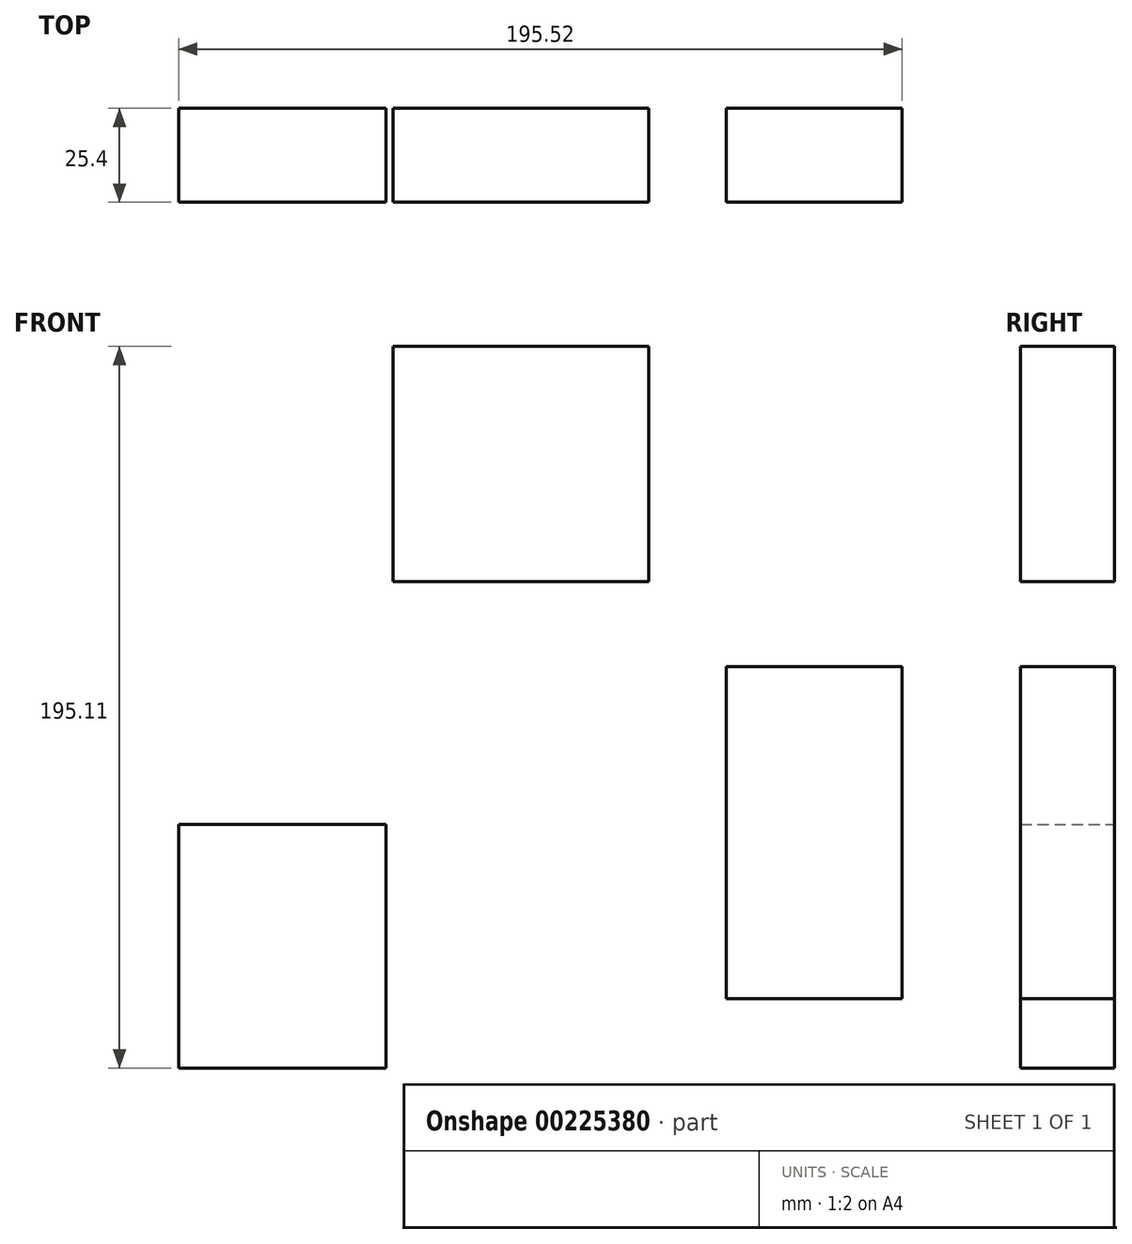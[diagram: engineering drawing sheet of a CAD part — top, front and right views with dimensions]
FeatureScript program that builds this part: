
annotation { "Feature Type Name" : "Feature", "Feature Type Description" : "" }
export const myFeature = defineFeature(function(context is Context, id is Id, definition is map)
    precondition{}
    {
        {
            var Q0;
            Q0=qCreatedBy(makeId("Front.planeOp"),FACE);
            var sketch = newSketch(context, id + "F0", { "sketchPlane" : qUnion([Q0])});
            skLineSegment(sketch, "E0.bottom", {"start": v(-48, 100.66) * mm, "end": v(21, 100.66) * mm});
            skLineSegment(sketch, "E0.top", {"start": v(-48, 37.07) * mm, "end": v(21, 37.07) * mm});
            skLineSegment(sketch, "E0.left", {"start": v(-48, 100.66) * mm, "end": v(-48, 37.07) * mm});
            skLineSegment(sketch, "E0.right", {"start": v(21, 100.66) * mm, "end": v(21, 37.07) * mm});
            skLineSegment(sketch, "E1.bottom", {"start": v(-106.01, -28.6) * mm, "end": v(-50, -28.6) * mm});
            skLineSegment(sketch, "E1.top", {"start": v(-106.01, -94.45) * mm, "end": v(-50, -94.45) * mm});
            skLineSegment(sketch, "E1.left", {"start": v(-106.01, -28.6) * mm, "end": v(-106.01, -94.45) * mm});
            skLineSegment(sketch, "E1.right", {"start": v(-50, -28.6) * mm, "end": v(-50, -94.45) * mm});
            skLineSegment(sketch, "E2.bottom", {"start": v(42, 14.13) * mm, "end": v(89.51, 14.13) * mm});
            skLineSegment(sketch, "E2.top", {"start": v(42, -75.67) * mm, "end": v(89.51, -75.67) * mm});
            skLineSegment(sketch, "E2.left", {"start": v(42, 14.13) * mm, "end": v(42, -75.67) * mm});
            skLineSegment(sketch, "E2.right", {"start": v(89.51, 14.13) * mm, "end": v(89.51, -75.67) * mm});
            skSolve(sketch);
        }
        {
            var Q0;
            Q0 = qSketchRegion(id + "F0", true);
            extrude(context, id + "F1", {"entities" : qUnion([Q0]), "depth" : 25.4 * mm});
        }
    });
